FCSTD DOCUMENT  (FreeCAD 0.20R26155 (Git))
Label: antenna-300-500MHz
License: All rights reserved
LicenseURL: http://en.wikipedia.org/wiki/All_rights_reserved
objects: Sketcher::SketchObject×2, App::DocumentObjectGroup×1
note: 2 computed .brp shape members not serialized (recipe doc carries the construction recipe); baked Part::Feature solids carry a one-line shape summary decoded from their .brp

FEATURE [Sketcher::SketchObject] Sketch  label="Pads_Poly"
  FullyConstrained = true
  sketch-geometry (18):
    g0: LineSegment StartX=0 StartY=1.016 StartZ=0 EndX=0 EndY=12.065 EndZ=0
    g1: LineSegment StartX=0 StartY=12.065 StartZ=0 EndX=2.032 EndY=14.097 EndZ=0
    g2: LineSegment StartX=2.032 StartY=14.097 StartZ=0 EndX=28.956 EndY=14.097 EndZ=0
    g3: LineSegment StartX=28.956 StartY=14.097 StartZ=0 EndX=30.988 EndY=12.065 EndZ=0
    g4: LineSegment StartX=30.988 StartY=12.065 StartZ=0 EndX=30.988 EndY=1.27 EndZ=0
    g5: ArcOfCircle CenterX=29.972 CenterY=1.27 CenterZ=0 NormalX=0 NormalY=0 NormalZ=1 AngleXU=0 Radius=1.016 StartAngle=3.14159 EndAngle=6.28319
    g6: LineSegment StartX=28.956 StartY=1.27 StartZ=0 EndX=28.956 EndY=11.2233 EndZ=0
    g7: LineSegment StartX=2.032 StartY=11.2233 StartZ=0 EndX=2.032 EndY=1.016 EndZ=0
    g8: LineSegment StartX=2.032 StartY=11.2233 StartZ=0 EndX=2.87368 EndY=12.065 EndZ=0
    g9: LineSegment StartX=2.87368 StartY=12.065 StartZ=0 EndX=28.1143 EndY=12.065 EndZ=0
    g10: LineSegment StartX=28.1143 StartY=12.065 StartZ=0 EndX=28.956 EndY=11.2233 EndZ=0
    g11: LineSegment StartX=0 StartY=13.081 StartZ=0 EndX=29.972 EndY=13.081 EndZ=0
    g12: LineSegment StartX=1.016 StartY=1.016 StartZ=0 EndX=1.016 EndY=13.081 EndZ=0
    g13: LineSegment StartX=29.972 StartY=1.27 StartZ=0 EndX=29.972 EndY=13.081 EndZ=0
    g14: LineSegment StartX=1.016 StartY=13.081 StartZ=0 EndX=2.45284 EndY=11.6442 EndZ=0
    g15: LineSegment StartX=29.972 StartY=13.081 StartZ=0 EndX=28.5352 EndY=11.6442 EndZ=0
    g16: Circle CenterX=29.972 CenterY=1.27 CenterZ=0 NormalX=0 NormalY=0 NormalZ=1 AngleXU=0 Radius=0.635
    g17: LineSegment StartX=0 StartY=1.016 StartZ=0 EndX=2.032 EndY=1.016 EndZ=0
  constraints (52):
    c: PointOnObject(g0,g-2)
    c: PointOnObject(g0,g-2)
    c: Coincident(g0,g1)
    c: Coincident(g1,g2)
    c: Horizontal(g2)
    c: Coincident(g2,g3)
    c: Coincident(g3,g4)
    c: Vertical(g4)
    c: Tangent(g4,g5) = 1.5708
    c: Vertical(g6)
    c: Vertical(g7)
    c: Tangent(g5,g6) = 1.5708
    c: Coincident(g7,g8)
    c: Coincident(g8,g9)
    c: Horizontal(g9)
    c: Coincident(g9,g10)
    c: Coincident(g10,g6)
    c: Parallel(g3,g10)
    c: Parallel(g1,g8)
    c: Angle(g-2,g1) = 2.35619
    c: Angle(g3,g4) = 2.35619
    c: PointOnObject(g11,g-2)
    c: PointOnObject(g11,g3)
    c: Horizontal(g11)
    c: Equal(g8,g10)
    c: Equal(g3,g1)
    c: DistanceY(g8,g1) = 2.032
    c: DistanceY(g8,g11) = 1.016
    c: PointOnObject(g12,g11)
    c: Vertical(g12)
    c: Coincident(g13,g5)
    c: Vertical(g13)
    c: DistanceY(g13,g13) = 11.811
    c: Coincident(g11,g13)
    c: Coincident(g14,g12)
    c: PointOnObject(g14,g8)
    c: Coincident(g15,g11)
    c: PointOnObject(g15,g10)
    c: Perpendicular(g10,g15)
    c: Perpendicular(g8,g14)
    c: Distance(g14) = 2.032
    c: Coincident(g16,g5)
    c: Radius(g16) = 0.635
    c: Coincident(g17,g0)
    c: Coincident(g17,g7)
    c: Horizontal(g17)
    c: Symmetric(g17,g17,g12)
    c: DistanceY(g12,g12) = 12.065
    c: DistanceX(g17,g17) = 2.032
    c: Radius(g5) = 1.016
    c: DistanceY(g-1,g12) = 1.016
    c: DistanceX(g11,g11) = 29.972
FEATURE [Sketcher::SketchObject] Sketch001  label="Pads_TH_SMD"
  ExternalGeometry = -> [Sketch]
  FullyConstrained = true
  sketch-geometry (4):
    g0: LineSegment StartX=2.032 StartY=1.016 StartZ=0 EndX=0 EndY=1.016 EndZ=0
    g1: LineSegment StartX=0 StartY=1.016 StartZ=0 EndX=0 EndY=0 EndZ=0
    g2: LineSegment StartX=0 StartY=0 StartZ=0 EndX=2.032 EndY=0 EndZ=0
    g3: LineSegment StartX=2.032 StartY=0 StartZ=0 EndX=2.032 EndY=1.016 EndZ=0
  constraints (10):
    c: Coincident(g0,g1)
    c: Coincident(g1,g2)
    c: Coincident(g2,g3)
    c: Coincident(g3,g0)
    c: Horizontal(g0)
    c: Horizontal(g2)
    c: Vertical(g1)
    c: Vertical(g3)
    c: Coincident(g0,g-3)
    c: Coincident(g1,g-1)
FEATURE [App::DocumentObjectGroup] Group  label="antenna"
  Group = -> [Sketch001,Sketch]
